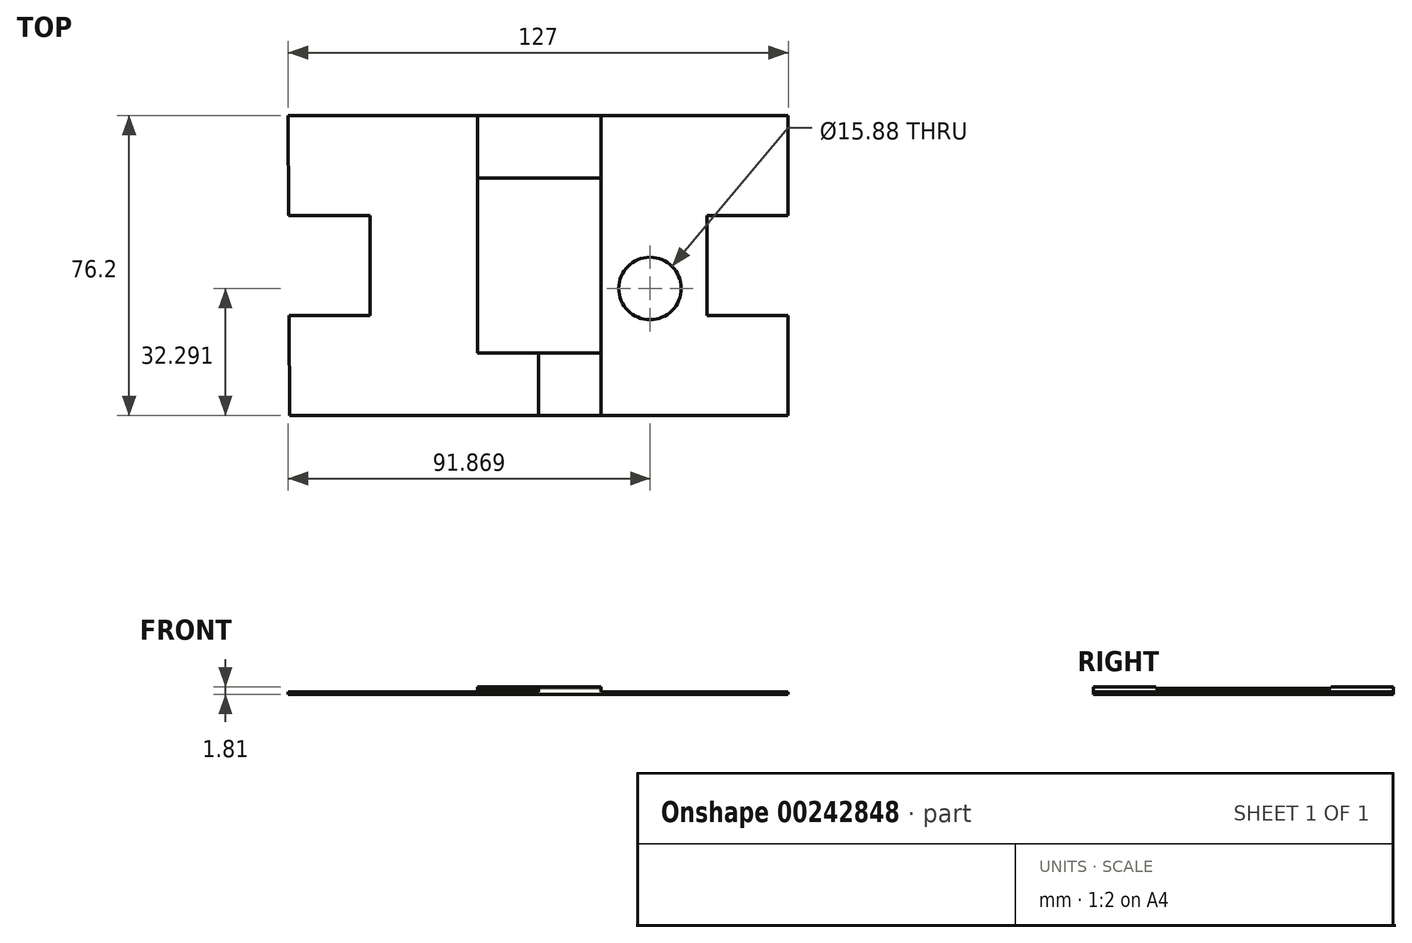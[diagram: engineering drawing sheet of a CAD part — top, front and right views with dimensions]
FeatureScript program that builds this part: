
annotation { "Feature Type Name" : "Feature", "Feature Type Description" : "" }
export const myFeature = defineFeature(function(context is Context, id is Id, definition is map)
    precondition{}
    {
        {
            var Q0;
            Q0=qCreatedBy(makeId("Top.planeOp"),FACE);
            var sketch = newSketch(context, id + "F0", { "sketchPlane" : qUnion([Q0])});
            skLineSegment(sketch, "E0", {"start": v(-154.93, 70.33) * mm, "end": v(-27.93, 70.33) * mm});
            skLineSegment(sketch, "E1", {"start": v(-27.93, 70.33) * mm, "end": v(-27.93, 44.93) * mm});
            skLineSegment(sketch, "E2", {"start": v(-27.93, -5.87) * mm, "end": v(-154.67, -5.87) * mm});
            skLineSegment(sketch, "E3", {"start": v(-154.67, -5.87) * mm, "end": v(-154.76, 19.53) * mm});
            skLineSegment(sketch, "E4", {"start": v(-27.93, 19.53) * mm, "end": v(-48.57, 19.53) * mm});
            skLineSegment(sketch, "E5", {"start": v(-48.57, 19.53) * mm, "end": v(-48.57, 44.93) * mm});
            skLineSegment(sketch, "E6", {"start": v(-48.57, 44.93) * mm, "end": v(-27.93, 44.93) * mm});
            skLineSegment(sketch, "E7", {"start": v(-154.85, 44.93) * mm, "end": v(-134.21, 45) * mm});
            skLineSegment(sketch, "E8", {"start": v(-134.21, 45) * mm, "end": v(-134.12, 19.6) * mm});
            skLineSegment(sketch, "E9", {"start": v(-134.12, 19.6) * mm, "end": v(-154.76, 19.53) * mm});
            skLineSegment(sketch, "E10", {"start": v(-48.57, 19.53) * mm, "end": v(-27.93, 19.53) * mm});
            skLineSegment(sketch, "E11.trimOffspring", {"start": v(-27.93, 19.53) * mm, "end": v(-27.93, -5.87) * mm});
            skLineSegment(sketch, "E12", {"start": v(-154.93, 70.33) * mm, "end": v(-154.85, 44.93) * mm});
            skSolve(sketch);
        }
        {
            var Q0;
            Q0=makeQuery(id+"F0.imprint","IMPRINT",FACE,{"disambiguationData":[TD([[makeQuery(id+"F0.imprint","IMPRINT",EDGE,{"derivedFrom":sQuery(id+"F0.wireOp",EDGE,"E0")}),-1.0]])]});
            extrude(context, id + "F1", {"entities" : qUnion([Q0]), "depth" : ((1 + 1 / 4) / 2) * mm});
        }
        {
            var Q0;
            Q0=makeQuery(id+"F1.opExtrude","CAP_FACE",FACE,{"disambiguationData":[OSD([sQuery(id+"F0.wireOp",EDGE,"E0"),sQuery(id+"F0.wireOp",EDGE,"E1"),sQuery(id+"F0.wireOp",EDGE,"E2"),sQuery(id+"F0.wireOp",EDGE,"E3"),sQuery(id+"F0.wireOp",EDGE,"E5"),sQuery(id+"F0.wireOp",EDGE,"E7"),sQuery(id+"F0.wireOp",EDGE,"E8"),sQuery(id+"F0.wireOp",EDGE,"E9"),sQuery(id+"F0.wireOp",EDGE,"E6"),sQuery(id+"F0.wireOp",EDGE,"E10"),sQuery(id+"F0.wireOp",EDGE,"E11.trimOffspring"),sQuery(id+"F0.wireOp",EDGE,"E12")])],"isStart":false});
            var sketch = newSketch(context, id + "F2", { "sketchPlane" : qUnion([Q0])});
            skLineSegment(sketch, "E13", {"start": v(-91.34, -5.87) * mm, "end": v(-91.34, 70.33) * mm});
            skLineSegment(sketch, "E14", {"start": v(-91.34, 70.33) * mm, "end": v(-91.01, 70.33) * mm});
            skLineSegment(sketch, "E15", {"start": v(-91.01, 70.33) * mm, "end": v(-91.01, -5.87) * mm});
            skLineSegment(sketch, "E16", {"start": v(-91.01, -5.87) * mm, "end": v(-91.34, -5.87) * mm});
            skLineSegment(sketch, "E17", {"start": v(-75.46, -5.87) * mm, "end": v(-75.46, 70.33) * mm});
            skLineSegment(sketch, "E18", {"start": v(-106.89, 70.33) * mm, "end": v(-75.46, 70.33) * mm});
            skLineSegment(sketch, "E19", {"start": v(-106.89, 70.33) * mm, "end": v(-106.89, -5.87) * mm});
            skLineSegment(sketch, "E20", {"start": v(-75.46, -5.87) * mm, "end": v(-106.89, -5.87) * mm});
            skLineSegment(sketch, "E21", {"start": v(-106.89, 10) * mm, "end": v(-91.01, 10) * mm});
            skLineSegment(sketch, "E22", {"start": v(-106.89, 54.45) * mm, "end": v(-91.01, 54.45) * mm});
            skLineSegment(sketch, "E23", {"start": v(-91.34, 54.45) * mm, "end": v(-75.46, 54.45) * mm});
            skLineSegment(sketch, "E24", {"start": v(-91.34, 10) * mm, "end": v(-75.46, 10) * mm});
            skLineSegment(sketch, "E25", {"start": v(-154.67, -5.87) * mm, "end": v(-91.17, -5.87) * mm});
            skLineSegment(sketch, "E26", {"start": v(-75.46, -5.87) * mm, "end": v(-75.46, 32.23) * mm});
            skCircle(sketch, "E27", {"center": v(-63.06, 26.42) * mm, "radius": 7.94 * mm});
            skSolve(sketch);
        }
        {
            var Q0;
            {var subQ1=sQuery(id+"F2.wireOp",EDGE,"E23");Q0=makeQuery(id+"F2.imprint","IMPRINT",FACE,{"disambiguationData":[TD([[makeQuery(id+"F2.imprint","IMPRINT",EDGE,{"derivedFrom":subQ1}),-1.0]])]});}
            var Q1;
            {var subQ0=sQuery(id+"F2.wireOp",EDGE,"E21");Q1=makeQuery(id+"F2.imprint","IMPRINT",FACE,{"disambiguationData":[TD([[makeQuery(id+"F2.imprint","IMPRINT",EDGE,{"derivedFrom":subQ0}),1.0]])]});}
            extrude(context, id + "F3", {"entities" : qUnion([Q0, Q1]), "operationType" : NewBodyOperationType.ADD, "depth" : (((3 + 5 / 8) - (1 + 1 / 4) - (3 / 4)) / 2) * mm});
        }
        {
            var Q0;
            {var subQ11=sQuery(id+"F2.wireOp",EDGE,"E18");Q0=makeQuery(id+"F2.imprint","IMPRINT",FACE,{"disambiguationData":[TD([[makeQuery(id+"F2.imprint","IMPRINT",EDGE,{"derivedFrom":subQ11}),-1.0]])]});}
            extrude(context, id + "F4", {"entities" : qUnion([Q0]), "operationType" : NewBodyOperationType.ADD, "depth" : (((3 + 5 / 8) - (1 + 1 / 4) - (1 + 1 / 2)) / 2) * mm});
        }
        {
            var Q0;
            {var subQ3=sQuery(id+"F2.wireOp",EDGE,"E23");Q0=makeQuery(id+"F2.imprint","IMPRINT",FACE,{"disambiguationData":[TD([[makeQuery(id+"F2.imprint","IMPRINT",EDGE,{"derivedFrom":subQ3}),1.0]])]});}
            var Q1;
            {var subQ5=sQuery(id+"F2.wireOp",EDGE,"E22");Q1=makeQuery(id+"F2.imprint","IMPRINT",FACE,{"disambiguationData":[TD([[makeQuery(id+"F2.imprint","IMPRINT",EDGE,{"derivedFrom":subQ5}),1.0]])]});}
            var Q2;
            {var subQ0=sQuery(id+"F2.wireOp",EDGE,"E16");Q2=makeQuery(id+"F2.imprint","IMPRINT",FACE,{"disambiguationData":[TD([[makeQuery(id+"F2.imprint","IMPRINT",EDGE,{"derivedFrom":subQ0}),-1.0]])]});}
            var Q3;
            {var subQ3=sQuery(id+"F2.wireOp",EDGE,"E24");Q3=makeQuery(id+"F2.imprint","IMPRINT",FACE,{"disambiguationData":[TD([[makeQuery(id+"F2.imprint","IMPRINT",EDGE,{"derivedFrom":subQ3}),-1.0]])]});}
            extrude(context, id + "F5", {"entities" : qUnion([Q0, Q1, Q2, Q3]), "operationType" : NewBodyOperationType.ADD, "depth" : (((3 + 5 / 8) - (1 + 1 / 4)) / 2) * mm});
        }
        {
            var Q0;
            Q0=makeQuery(id+"F2.imprint","IMPRINT",FACE,{"disambiguationData":[TD([[makeQuery(id+"F2.imprint","IMPRINT",EDGE,{"derivedFrom":sQuery(id+"F2.wireOp",EDGE,"E27")}),1.0]])]});
            extrude(context, id + "F6", {"entities" : qUnion([Q0]), "operationType" : NewBodyOperationType.REMOVE, "endBound" : BoundingType.THROUGH_ALL, "oppositeDirection" : true, "depth" : 25.4 * mm});
        }
    });
